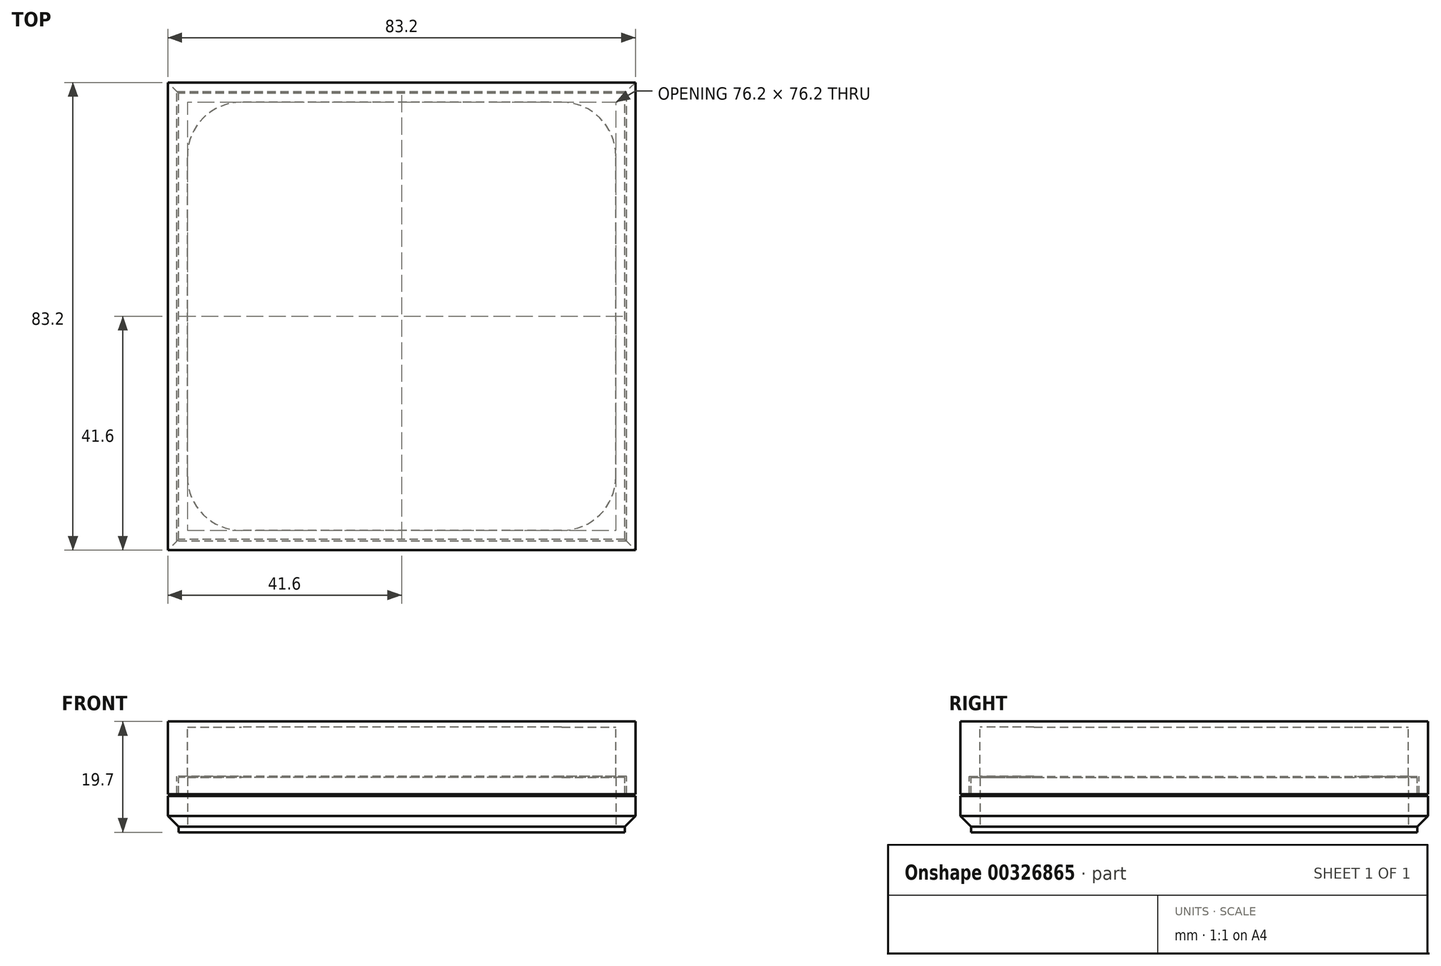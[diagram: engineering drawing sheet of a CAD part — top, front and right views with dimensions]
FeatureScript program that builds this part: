
annotation { "Feature Type Name" : "Feature", "Feature Type Description" : "" }
export const myFeature = defineFeature(function(context is Context, id is Id, definition is map)
    precondition{}
    {
        {
            assignVariable(context, id + "F0", {"name" : "chaff", "anyValue" : .3});
        }
        {
            assignVariable(context, id + "F1", {"name" : "basethick", "anyValue" : 1});
        }
        {
            assignVariable(context, id + "F2", {"name" : "diskdiam", "anyValue" : 18.6});
        }
        {
            assignVariable(context, id + "F3", {"name" : "fiveTokenHeight", "anyValue" : 16.3});
        }
        {
            assignVariable(context, id + "F4", {"name" : "lidrimdepth", "anyValue" : 3});
        }
        {
            var Q0;
            Q0=qCreatedBy(makeId("Top.planeOp"),FACE);
            var sketch = newSketch(context, id + "F5", { "sketchPlane" : qUnion([Q0])});
            skLineSegment(sketch, "E0.bottom", {"start": v(41.6, -41.6) * mm, "end": v(-41.6, -41.6) * mm});
            skLineSegment(sketch, "E0.top", {"start": v(41.6, 41.6) * mm, "end": v(-41.6, 41.6) * mm});
            skLineSegment(sketch, "E0.left", {"start": v(41.6, -41.6) * mm, "end": v(41.6, 41.6) * mm});
            skLineSegment(sketch, "E0.right", {"start": v(-41.6, -41.6) * mm, "end": v(-41.6, 41.6) * mm});
            skPoint(sketch, "E0.middle", {"position": v(0, 0) * mm});
            skSolve(sketch);
        }
        {
            var Q0;
            Q0=qSketchRegion(id+"F5",true);
            extrude(context, id + "F6", {"entities" : qUnion([Q0]), "depth" : (getVariable(context, 'basethick')) * mm});
        }
        {
            var Q0;
            Q0=makeQuery(id+"F6.opExtrude","CAP_FACE",FACE,{"disambiguationData":[OSD([sQuery(id+"F5.wireOp",EDGE,"E0.bottom"),sQuery(id+"F5.wireOp",EDGE,"E0.top"),sQuery(id+"F5.wireOp",EDGE,"E0.left"),sQuery(id+"F5.wireOp",EDGE,"E0.right")])],"isStart":false});
            var sketch = newSketch(context, id + "F7", { "sketchPlane" : qUnion([Q0])});
            skLineSegment(sketch, "E1.bottom", {"start": v(38.1, -38.1) * mm, "end": v(-38.1, -38.1) * mm});
            skLineSegment(sketch, "E1.top", {"start": v(38.1, 38.1) * mm, "end": v(-38.1, 38.1) * mm});
            skLineSegment(sketch, "E1.left", {"start": v(38.1, -38.1) * mm, "end": v(38.1, 38.1) * mm});
            skLineSegment(sketch, "E1.right", {"start": v(-38.1, -38.1) * mm, "end": v(-38.1, 38.1) * mm});
            skPoint(sketch, "E1.middle", {"position": v(0, 0) * mm});
            skLineSegment(sketch, "E2", {"start": v(-41.6, 0) * mm, "end": v(-38.1, 0) * mm, "construction": true});
            skLineSegment(sketch, "E3", {"start": v(0, 38.1) * mm, "end": v(0, 41.6) * mm, "construction": true});
            skLineSegment(sketch, "E4.0", {"start": v(-41.6, -41.6) * mm, "end": v(-41.6, 41.6) * mm});
            skLineSegment(sketch, "E5.0", {"start": v(41.6, -41.6) * mm, "end": v(-41.6, -41.6) * mm});
            skLineSegment(sketch, "E6.0", {"start": v(41.6, -41.6) * mm, "end": v(41.6, 41.6) * mm});
            skLineSegment(sketch, "E7.0", {"start": v(41.6, 41.6) * mm, "end": v(-41.6, 41.6) * mm});
            skSolve(sketch);
        }
        {
            var Q0;
            Q0=qSketchRegion(id+"F7",true);
            extrude(context, id + "F8", {"entities" : qUnion([Q0]), "operationType" : NewBodyOperationType.ADD, "depth" : (getVariable(context, 'fiveTokenHeight') / 2 + getVariable(context, 'chaff') * 2) * mm});
        }
        {
            var Q0;
            {var subQ0=sQuery(id+"FkSYW39zBoowpRB_1.wireOp",EDGE,"b7063ba6-163c-4e90-9692-3a0a1676d49b.0");var subQ1=sQuery(id+"FkSYW39zBoowpRB_1.wireOp",EDGE,"5b0bd29a-2a72-4641-92b4-ce3cebaaf724.1.0.1");var subQ2=sQuery(id+"FkSYW39zBoowpRB_1.wireOp",EDGE,"5b0bd29a-2a72-4641-92b4-ce3cebaaf724.2.0.1");Q0=makeQuery(id+"FKPirlnXY4BgwBl_1.boolean.opBoolean","MERGE",FACE,{"derivedFrom":[makeQuery(id+"F8.opExtrude","CAP_FACE",FACE,{"disambiguationData":[OSD([sQuery(id+"F7.wireOp",EDGE,"E1.bottom"),sQuery(id+"F7.wireOp",EDGE,"E1.top"),sQuery(id+"F7.wireOp",EDGE,"E1.left"),sQuery(id+"F7.wireOp",EDGE,"E1.right"),sQuery(id+"F7.wireOp",EDGE,"E4.0"),sQuery(id+"F7.wireOp",EDGE,"E5.0"),sQuery(id+"F7.wireOp",EDGE,"E6.0"),sQuery(id+"F7.wireOp",EDGE,"E7.0")])],"isStart":false}),makeQuery(id+"FKPirlnXY4BgwBl_1.opExtrude","SWEPT_FACE",FACE,{"disambiguationData":[OSD([subQ0]),TDD([makeQuery(id+"FkSYW39zBoowpRB_1.imprint","IMPRINT",EDGE,{"disambiguationData":[TD([[makeQuery(id+"FkSYW39zBoowpRB_1.imprint","INTERSECT",VERTEX,{"derivedFrom":[sQuery(id+"FkSYW39zBoowpRB_1.wireOp",EDGE,"ed8556cc-012e-414f-a647-4d99696943b9.0"),subQ0]}),-1.0]])],"derivedFrom":subQ0})])]}),makeQuery(id+"FKPirlnXY4BgwBl_1.opExtrude","SWEPT_FACE",FACE,{"disambiguationData":[OSD([subQ0]),TDD([makeQuery(id+"FkSYW39zBoowpRB_1.imprint","IMPRINT",EDGE,{"disambiguationData":[TD([[makeQuery(id+"FkSYW39zBoowpRB_1.imprint","INTERSECT",VERTEX,{"disambiguationData":[OD(1.0)],"derivedFrom":[subQ2,subQ0]}),1.0]])],"derivedFrom":subQ0})])]}),makeQuery(id+"FKPirlnXY4BgwBl_1.opExtrude","SWEPT_FACE",FACE,{"disambiguationData":[OSD([subQ0]),TDD([makeQuery(id+"FkSYW39zBoowpRB_1.imprint","IMPRINT",EDGE,{"disambiguationData":[TD([[makeQuery(id+"FkSYW39zBoowpRB_1.imprint","INTERSECT",VERTEX,{"disambiguationData":[OD(1.0)],"derivedFrom":[subQ1,subQ0]}),1.0]])],"derivedFrom":subQ0})])]}),makeQuery(id+"FKPirlnXY4BgwBl_1.opExtrude","SWEPT_FACE",FACE,{"disambiguationData":[OSD([subQ0]),TDD([makeQuery(id+"FkSYW39zBoowpRB_1.imprint","IMPRINT",EDGE,{"disambiguationData":[TD([[makeQuery(id+"FkSYW39zBoowpRB_1.imprint","INTERSECT",VERTEX,{"derivedFrom":[sQuery(id+"FkSYW39zBoowpRB_1.wireOp",EDGE,"CCxmkI6E-hdHg-CZTa-q9Gf-agiM700yoBqG"),subQ0]}),1.0]])],"derivedFrom":subQ0})])]})]});}
            cPlane(context, id + "F9", {"entities" : qUnion([Q0]), "cplaneType" : CPlaneType.OFFSET, "offset" : .1 * mm, "width" : 150 * mm, "height" : 150 * mm});
        }
        {
            var Q0;
            Q0=makeQuery(id+"F6.opExtrude","SWEPT_BODY",BODY,{"disambiguationData":[OSD([sQuery(id+"F5.wireOp",EDGE,"E0.bottom"),sQuery(id+"F5.wireOp",EDGE,"E0.top"),sQuery(id+"F5.wireOp",EDGE,"E0.left"),sQuery(id+"F5.wireOp",EDGE,"E0.right")])]});
            var Q1;
            Q1=qCreatedBy(id+"F9.planeOp",FACE);
            mirror(context, id + "F10", {"entities" : qUnion([Q0]), "mirrorPlane" : qUnion([Q1])});
        }
        {
            var Q0;
            {var subQ0=sQuery(id+"FkSYW39zBoowpRB_1.wireOp",EDGE,"b7063ba6-163c-4e90-9692-3a0a1676d49b.0");var subQ1=sQuery(id+"FkSYW39zBoowpRB_1.wireOp",EDGE,"5b0bd29a-2a72-4641-92b4-ce3cebaaf724.1.0.1");var subQ2=sQuery(id+"FkSYW39zBoowpRB_1.wireOp",EDGE,"5b0bd29a-2a72-4641-92b4-ce3cebaaf724.2.0.1");Q0=makeQuery(id+"FKPirlnXY4BgwBl_1.boolean.opBoolean","MERGE",FACE,{"derivedFrom":[makeQuery(id+"F8.opExtrude","CAP_FACE",FACE,{"disambiguationData":[OSD([sQuery(id+"F7.wireOp",EDGE,"E1.bottom"),sQuery(id+"F7.wireOp",EDGE,"E1.top"),sQuery(id+"F7.wireOp",EDGE,"E1.left"),sQuery(id+"F7.wireOp",EDGE,"E1.right"),sQuery(id+"F7.wireOp",EDGE,"E4.0"),sQuery(id+"F7.wireOp",EDGE,"E5.0"),sQuery(id+"F7.wireOp",EDGE,"E6.0"),sQuery(id+"F7.wireOp",EDGE,"E7.0")])],"isStart":false}),makeQuery(id+"FKPirlnXY4BgwBl_1.opExtrude","SWEPT_FACE",FACE,{"disambiguationData":[OSD([subQ0]),TDD([makeQuery(id+"FkSYW39zBoowpRB_1.imprint","IMPRINT",EDGE,{"disambiguationData":[TD([[makeQuery(id+"FkSYW39zBoowpRB_1.imprint","INTERSECT",VERTEX,{"derivedFrom":[sQuery(id+"FkSYW39zBoowpRB_1.wireOp",EDGE,"ed8556cc-012e-414f-a647-4d99696943b9.0"),subQ0]}),-1.0]])],"derivedFrom":subQ0})])]}),makeQuery(id+"FKPirlnXY4BgwBl_1.opExtrude","SWEPT_FACE",FACE,{"disambiguationData":[OSD([subQ0]),TDD([makeQuery(id+"FkSYW39zBoowpRB_1.imprint","IMPRINT",EDGE,{"disambiguationData":[TD([[makeQuery(id+"FkSYW39zBoowpRB_1.imprint","INTERSECT",VERTEX,{"disambiguationData":[OD(1.0)],"derivedFrom":[subQ2,subQ0]}),1.0]])],"derivedFrom":subQ0})])]}),makeQuery(id+"FKPirlnXY4BgwBl_1.opExtrude","SWEPT_FACE",FACE,{"disambiguationData":[OSD([subQ0]),TDD([makeQuery(id+"FkSYW39zBoowpRB_1.imprint","IMPRINT",EDGE,{"disambiguationData":[TD([[makeQuery(id+"FkSYW39zBoowpRB_1.imprint","INTERSECT",VERTEX,{"disambiguationData":[OD(1.0)],"derivedFrom":[subQ1,subQ0]}),1.0]])],"derivedFrom":subQ0})])]}),makeQuery(id+"FKPirlnXY4BgwBl_1.opExtrude","SWEPT_FACE",FACE,{"disambiguationData":[OSD([subQ0]),TDD([makeQuery(id+"FkSYW39zBoowpRB_1.imprint","IMPRINT",EDGE,{"disambiguationData":[TD([[makeQuery(id+"FkSYW39zBoowpRB_1.imprint","INTERSECT",VERTEX,{"derivedFrom":[sQuery(id+"FkSYW39zBoowpRB_1.wireOp",EDGE,"CCxmkI6E-hdHg-CZTa-q9Gf-agiM700yoBqG"),subQ0]}),1.0]])],"derivedFrom":subQ0})])]})]});}
            var sketch = newSketch(context, id + "F11", { "sketchPlane" : qUnion([Q0])});
            skLineSegment(sketch, "E8.0", {"start": v(41.6, 41.6) * mm, "end": v(-41.6, 41.6) * mm});
            skLineSegment(sketch, "E9.0", {"start": v(-41.6, -41.6) * mm, "end": v(-41.6, 41.6) * mm});
            skLineSegment(sketch, "E10.0", {"start": v(41.6, -41.6) * mm, "end": v(-41.6, -41.6) * mm});
            skLineSegment(sketch, "E11.0", {"start": v(41.6, -41.6) * mm, "end": v(41.6, 41.6) * mm});
            skLineSegment(sketch, "E12.0", {"start": v(39.7, 39.7) * mm, "end": v(-39.7, 39.7) * mm});
            skLineSegment(sketch, "E12.1", {"start": v(39.7, -39.7) * mm, "end": v(39.7, 39.7) * mm});
            skLineSegment(sketch, "E12.2", {"start": v(39.7, -39.7) * mm, "end": v(-39.7, -39.7) * mm});
            skLineSegment(sketch, "E12.3", {"start": v(-39.7, -39.7) * mm, "end": v(-39.7, 39.7) * mm});
            skSolve(sketch);
        }
        {
            var Q0;
            Q0=makeQuery(id+"F11.imprint","IMPRINT",FACE,{"disambiguationData":[TD([[makeQuery(id+"F11.imprint","IMPRINT",EDGE,{"derivedFrom":sQuery(id+"F11.wireOp",EDGE,"E8.0")}),1.0]])]});
            extrude(context, id + "F12", {"entities" : qUnion([Q0]), "operationType" : NewBodyOperationType.REMOVE, "oppositeDirection" : true, "depth" : (getVariable(context, 'lidrimdepth') + getVariable(context, 'chaff')) * mm});
        }
        {
            var Q0;
            Q0=makeQuery(id+"F6.opExtrude","CAP_FACE",FACE,{"disambiguationData":[OSD([sQuery(id+"F5.wireOp",EDGE,"E0.bottom"),sQuery(id+"F5.wireOp",EDGE,"E0.top"),sQuery(id+"F5.wireOp",EDGE,"E0.left"),sQuery(id+"F5.wireOp",EDGE,"E0.right")])],"isStart":true});
            var sketch = newSketch(context, id + "F13", { "sketchPlane" : qUnion([Q0])});
            skLineSegment(sketch, "E13.0", {"start": v(41.6, 41.6) * mm, "end": v(-41.6, 41.6) * mm});
            skLineSegment(sketch, "E14.0", {"start": v(-41.6, 41.6) * mm, "end": v(-41.6, -41.6) * mm});
            skLineSegment(sketch, "E15.0", {"start": v(41.6, 41.6) * mm, "end": v(41.6, -41.6) * mm});
            skLineSegment(sketch, "E16.0", {"start": v(41.6, -41.6) * mm, "end": v(-41.6, -41.6) * mm});
            skLineSegment(sketch, "E17.0", {"start": v(39.7, 39.7) * mm, "end": v(-39.7, 39.7) * mm});
            skLineSegment(sketch, "E17.1", {"start": v(39.7, 39.7) * mm, "end": v(39.7, -39.7) * mm});
            skLineSegment(sketch, "E17.2", {"start": v(39.7, -39.7) * mm, "end": v(-39.7, -39.7) * mm});
            skLineSegment(sketch, "E17.3", {"start": v(-39.7, 39.7) * mm, "end": v(-39.7, -39.7) * mm});
            skSolve(sketch);
        }
        {
            var Q0;
            Q0=qSketchRegion(id+"F13",true);
            extrude(context, id + "F14", {"entities" : qUnion([Q0]), "operationType" : NewBodyOperationType.REMOVE, "oppositeDirection" : true, "depth" : (getVariable(context, 'lidrimdepth')) * mm});
        }
        {
            var Q0;
            Q0=makeQuery(id+"F14.boolean.opBoolean","COPY",EDGE,{"derivedFrom":makeQuery(id+"F14.opExtrude","CAP_EDGE",EDGE,{"disambiguationData":[OSD([sQuery(id+"F13.wireOp",EDGE,"E17.0")])],"isStart":false})});
            var Q1;
            Q1=makeQuery(id+"F14.boolean.opBoolean","COPY",EDGE,{"derivedFrom":makeQuery(id+"F14.opExtrude","CAP_EDGE",EDGE,{"disambiguationData":[OSD([sQuery(id+"F13.wireOp",EDGE,"E17.3")])],"isStart":false})});
            var Q2;
            Q2=makeQuery(id+"F14.boolean.opBoolean","COPY",EDGE,{"derivedFrom":makeQuery(id+"F14.opExtrude","CAP_EDGE",EDGE,{"disambiguationData":[OSD([sQuery(id+"F13.wireOp",EDGE,"E17.2")])],"isStart":false})});
            var Q3;
            Q3=makeQuery(id+"F14.boolean.opBoolean","COPY",EDGE,{"derivedFrom":makeQuery(id+"F14.opExtrude","CAP_EDGE",EDGE,{"disambiguationData":[OSD([sQuery(id+"F13.wireOp",EDGE,"E17.1")])],"isStart":false})});
            chamfer(context, id + "F15", {"entities" : qUnion([Q0, Q1, Q2, Q3]), "width" : 2 * mm, "tangentPropagation" : true});
        }
        {
            var Q0;
            {var subQ0=sQuery(id+"FkSYW39zBoowpRB_1.wireOp",EDGE,"b7063ba6-163c-4e90-9692-3a0a1676d49b.0");var subQ1=sQuery(id+"FkSYW39zBoowpRB_1.wireOp",EDGE,"5b0bd29a-2a72-4641-92b4-ce3cebaaf724.1.0.1");var subQ2=sQuery(id+"FkSYW39zBoowpRB_1.wireOp",EDGE,"5b0bd29a-2a72-4641-92b4-ce3cebaaf724.2.0.1");Q0=makeQuery(id+"F10.opPattern","COPY",FACE,{"derivedFrom":makeQuery(id+"FKPirlnXY4BgwBl_1.boolean.opBoolean","MERGE",FACE,{"derivedFrom":[makeQuery(id+"F8.opExtrude","CAP_FACE",FACE,{"disambiguationData":[OSD([sQuery(id+"F7.wireOp",EDGE,"E1.bottom"),sQuery(id+"F7.wireOp",EDGE,"E1.top"),sQuery(id+"F7.wireOp",EDGE,"E1.left"),sQuery(id+"F7.wireOp",EDGE,"E1.right"),sQuery(id+"F7.wireOp",EDGE,"E4.0"),sQuery(id+"F7.wireOp",EDGE,"E5.0"),sQuery(id+"F7.wireOp",EDGE,"E6.0"),sQuery(id+"F7.wireOp",EDGE,"E7.0")])],"isStart":false}),makeQuery(id+"FKPirlnXY4BgwBl_1.opExtrude","SWEPT_FACE",FACE,{"disambiguationData":[OSD([subQ0]),TDD([makeQuery(id+"FkSYW39zBoowpRB_1.imprint","IMPRINT",EDGE,{"disambiguationData":[TD([[makeQuery(id+"FkSYW39zBoowpRB_1.imprint","INTERSECT",VERTEX,{"derivedFrom":[sQuery(id+"FkSYW39zBoowpRB_1.wireOp",EDGE,"ed8556cc-012e-414f-a647-4d99696943b9.0"),subQ0]}),-1.0]])],"derivedFrom":subQ0})])]}),makeQuery(id+"FKPirlnXY4BgwBl_1.opExtrude","SWEPT_FACE",FACE,{"disambiguationData":[OSD([subQ0]),TDD([makeQuery(id+"FkSYW39zBoowpRB_1.imprint","IMPRINT",EDGE,{"disambiguationData":[TD([[makeQuery(id+"FkSYW39zBoowpRB_1.imprint","INTERSECT",VERTEX,{"disambiguationData":[OD(1.0)],"derivedFrom":[subQ2,subQ0]}),1.0]])],"derivedFrom":subQ0})])]}),makeQuery(id+"FKPirlnXY4BgwBl_1.opExtrude","SWEPT_FACE",FACE,{"disambiguationData":[OSD([subQ0]),TDD([makeQuery(id+"FkSYW39zBoowpRB_1.imprint","IMPRINT",EDGE,{"disambiguationData":[TD([[makeQuery(id+"FkSYW39zBoowpRB_1.imprint","INTERSECT",VERTEX,{"disambiguationData":[OD(1.0)],"derivedFrom":[subQ1,subQ0]}),1.0]])],"derivedFrom":subQ0})])]}),makeQuery(id+"FKPirlnXY4BgwBl_1.opExtrude","SWEPT_FACE",FACE,{"disambiguationData":[OSD([subQ0]),TDD([makeQuery(id+"FkSYW39zBoowpRB_1.imprint","IMPRINT",EDGE,{"disambiguationData":[TD([[makeQuery(id+"FkSYW39zBoowpRB_1.imprint","INTERSECT",VERTEX,{"derivedFrom":[sQuery(id+"FkSYW39zBoowpRB_1.wireOp",EDGE,"CCxmkI6E-hdHg-CZTa-q9Gf-agiM700yoBqG"),subQ0]}),1.0]])],"derivedFrom":subQ0})])]})]}),"instanceName":"1"});}
            var sketch = newSketch(context, id + "F16", { "sketchPlane" : qUnion([Q0])});
            skPoint(sketch, "E18.0", {"position": v(-38.1, 38.1) * mm});
            skPoint(sketch, "E19.0", {"position": v(-38.1, -38.1) * mm});
            skLineSegment(sketch, "E20", {"start": v(-38.1, 38.1) * mm, "end": v(-38.1, -38.1) * mm, "construction": true});
            skLineSegment(sketch, "E21.0", {"start": v(40, 40) * mm, "end": v(-40, 40) * mm});
            skLineSegment(sketch, "E21.1", {"start": v(40, 40) * mm, "end": v(40, -40) * mm});
            skLineSegment(sketch, "E21.2", {"start": v(-40, -40) * mm, "end": v(40, -40) * mm});
            skLineSegment(sketch, "E21.3", {"start": v(-40, 40) * mm, "end": v(-40, -40) * mm});
            skLineSegment(sketch, "E22.0", {"start": v(41.6, 41.6) * mm, "end": v(-41.6, 41.6) * mm});
            skLineSegment(sketch, "E23.0", {"start": v(41.6, 41.6) * mm, "end": v(41.6, -41.6) * mm});
            skLineSegment(sketch, "E24.0", {"start": v(41.6, -41.6) * mm, "end": v(-41.6, -41.6) * mm});
            skLineSegment(sketch, "E25.0", {"start": v(-41.6, 41.6) * mm, "end": v(-41.6, -41.6) * mm});
            skPoint(sketch, "E26", {"position": v(38.1, 38.1) * mm});
            skPoint(sketch, "E27", {"position": v(38.1, -38.1) * mm});
            skLineSegment(sketch, "E28", {"start": v(-38.1, 38.1) * mm, "end": v(38.1, 38.1) * mm, "construction": true});
            skLineSegment(sketch, "E29", {"start": v(-38.1, -38.1) * mm, "end": v(38.1, -38.1) * mm, "construction": true});
            skLineSegment(sketch, "E30", {"start": v(0, 40) * mm, "end": v(0, 38.1) * mm, "construction": true});
            skLineSegment(sketch, "E31", {"start": v(-40, 0) * mm, "end": v(-38.1, 0) * mm, "construction": true});
            skSolve(sketch);
        }
        {
            var Q0;
            Q0=qSketchRegion(id+"F16",true);
            extrude(context, id + "F17", {"entities" : qUnion([Q0]), "operationType" : NewBodyOperationType.ADD, "depth" : 3.2 * mm});
        }
        {
            var Q0;
            Q0=makeQuery(id+"F8.opExtrude","SWEPT_EDGE",EDGE,{"disambiguationData":[OSD([sQuery(id+"F7.wireOp",EDGE,"E1.top"),sQuery(id+"F7.wireOp",EDGE,"E1.right")])]});
            var Q1;
            Q1=makeQuery(id+"F8.opExtrude","SWEPT_EDGE",EDGE,{"disambiguationData":[OSD([sQuery(id+"F7.wireOp",EDGE,"E1.top"),sQuery(id+"F7.wireOp",EDGE,"E1.left")])]});
            var Q2;
            Q2=makeQuery(id+"F8.opExtrude","SWEPT_EDGE",EDGE,{"disambiguationData":[OSD([sQuery(id+"F7.wireOp",EDGE,"E1.bottom"),sQuery(id+"F7.wireOp",EDGE,"E1.right")])]});
            var Q3;
            Q3=makeQuery(id+"F8.opExtrude","SWEPT_EDGE",EDGE,{"disambiguationData":[OSD([sQuery(id+"F7.wireOp",EDGE,"E1.bottom"),sQuery(id+"F7.wireOp",EDGE,"E1.left")])]});
            var Q4;
            Q4=makeQuery(id+"F10.opPattern","COPY",EDGE,{"derivedFrom":makeQuery(id+"F8.opExtrude","SWEPT_EDGE",EDGE,{"disambiguationData":[OSD([sQuery(id+"F7.wireOp",EDGE,"E1.bottom"),sQuery(id+"F7.wireOp",EDGE,"E1.right")])]}),"instanceName":"1"});
            var Q5;
            Q5=makeQuery(id+"F10.opPattern","COPY",EDGE,{"derivedFrom":makeQuery(id+"F8.opExtrude","SWEPT_EDGE",EDGE,{"disambiguationData":[OSD([sQuery(id+"F7.wireOp",EDGE,"E1.bottom"),sQuery(id+"F7.wireOp",EDGE,"E1.left")])]}),"instanceName":"1"});
            var Q6;
            Q6=makeQuery(id+"F10.opPattern","COPY",EDGE,{"derivedFrom":makeQuery(id+"F8.opExtrude","SWEPT_EDGE",EDGE,{"disambiguationData":[OSD([sQuery(id+"F7.wireOp",EDGE,"E1.top"),sQuery(id+"F7.wireOp",EDGE,"E1.left")])]}),"instanceName":"1"});
            var Q7;
            Q7=makeQuery(id+"F10.opPattern","COPY",EDGE,{"derivedFrom":makeQuery(id+"F8.opExtrude","SWEPT_EDGE",EDGE,{"disambiguationData":[OSD([sQuery(id+"F7.wireOp",EDGE,"E1.top"),sQuery(id+"F7.wireOp",EDGE,"E1.right")])]}),"instanceName":"1"});
            fillet(context, id + "F18", {"entities" : qUnion([Q0, Q1, Q2, Q3, Q4, Q5, Q6, Q7]), "radius" : (getVariable(context, 'diskdiam') / 2 + getVariable(context, 'chaff')) * mm, "tangentPropagation" : true, "allowEdgeOverflow" : false});
        }
    });
